# Revit family: QF_Hugentobler_Holdomat_711
name_source: partatom
category: Sonderausstattung
revit_build: Autodesk Revit 2018 (Build: 20190510_1515(x64)
units: mm (PartAtom-declared; Revit-internal decimal feet)

## family parameters
Arbeitsebenenbasiert = Ja
Beim Laden mit Abzugskörper schneiden = Nein
Bemaßung runder Anschluss = Durchmesser verwenden
Gemeinsam genutzt = Ja
Immer vertikal = Ja
OmniClass-Nummer = 23.40.40.14.17.31
OmniClass-Titel = Small Specialized Cooking Equipment
Raumberechnungspunkt = Nein
Teiletyp = Normal

## types (1)
- 1NAC - 230V - 50 Hz
    Anzahl der Pole = 3
    Bauelement = E1090320
    Baugruppenkennzeichen = E1090320
    Beschreibung = Warmhalte- und Niedertemperaturgargerät
    Betriebsstrom = 0 A
    Direkte Abwärme = 0 W
    Elektrische leistung = 1800 W
    Fließstrom = 0 A
    Frequenz = 50 Hz
    Gebäudeleittechnik mit digitale Schnittstelle = Nein
    Gerätegewicht Netto = 38.00 kg
    Hauptschalter integriert = Nein
    Hersteller = Hugentobler
    Höhe = 346 mm  [stored 1.13517 ft]
    Internetadresse Gerätehersteller = www.hugentobler.com
    Internetadresse für Ersatzteilliste = www.hugentobler.com
    Internetadresse für die Maßzeichnung = www.hugentobler.com
    Internetadresse für kritische Ersatzteilliste = www.hugentobler.com
    Lastfreie Zeichnung = Nein
    Latente Abwärme Belastung = 400 W
    Länge Gerätebreite = 416 mm
    Maximale Geräteabsicherung = 10 A
    Minimale Stromaufnahme = 7 A
    Modell = Hold-o-mat 711
    NAFEM Zulassungs ID Nummer = Keine
    Phasen = 1
    Potentialausgleich = Nein
    Scheinleistung = 0 VA
    Sensible Abwärme Belastung = 850 W
    Spannung = 230 V
    Spannungsfreier Anschluss = Nein
    Stecker System = T13
    Tiefe = 667 mm  [stored 2.18832 ft]
    Vorgabe-Ansicht = 1219 mm
    Zubehör = Nein
    Zuleitung zum Gerät im Lieferumfang = Ja

note: [stored X ft] marks values corroborated as IEEE doubles in the binary element streams (Revit-internal decimal feet)

## geometry (parser evidence)
native form markers: Extrusion x1
no freeform markers — native parametric forms only
